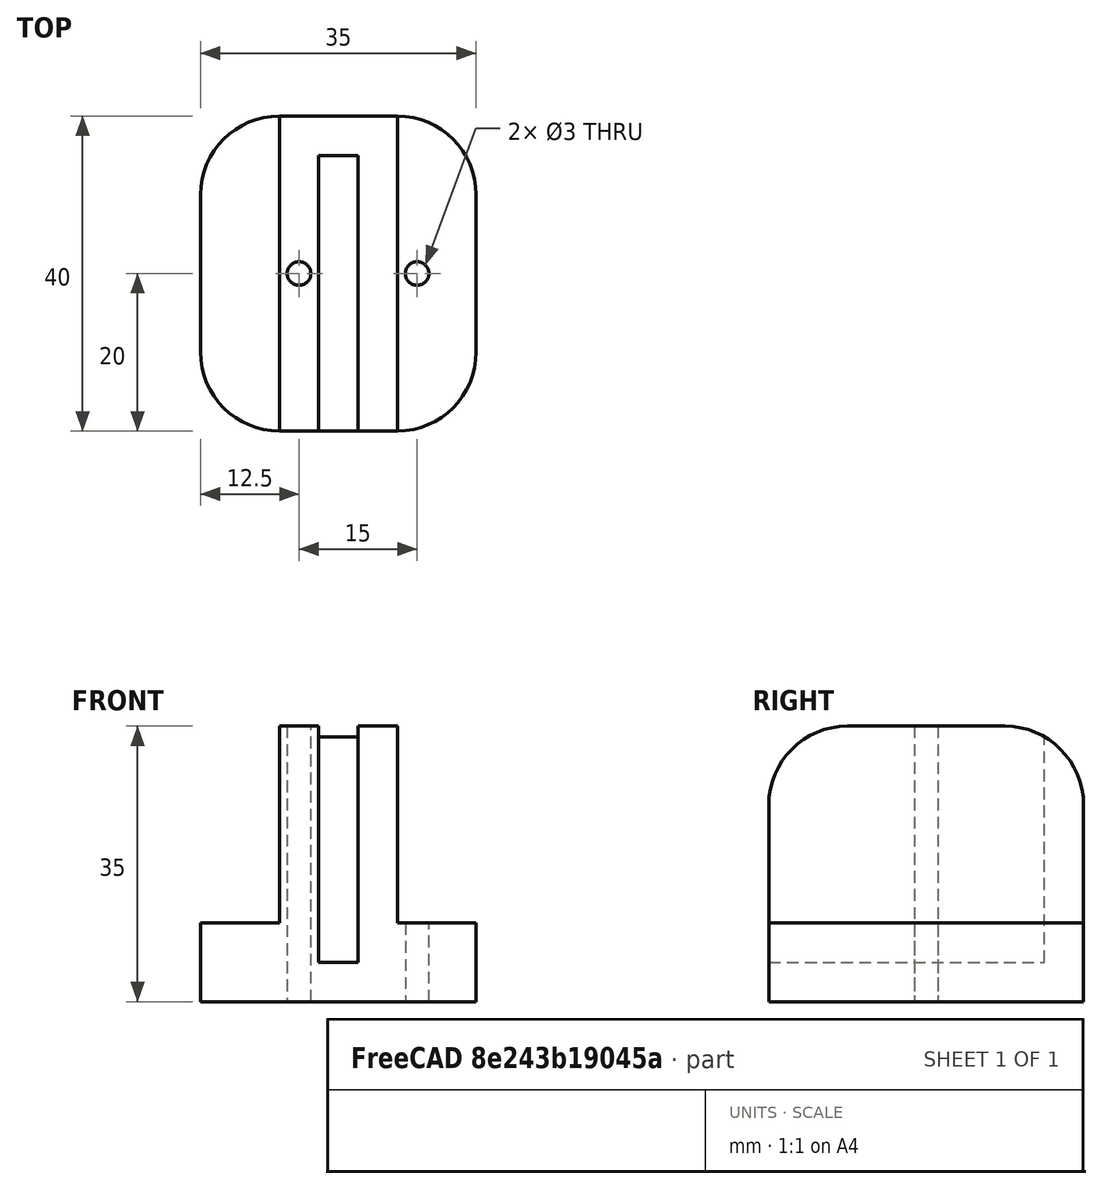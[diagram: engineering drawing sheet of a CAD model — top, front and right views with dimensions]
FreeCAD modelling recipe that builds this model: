
FCSTD DOCUMENT  (FreeCAD 0.21R33771 (Git))
Label: bidee-holder
License: All rights reserved
LicenseURL: https://en.wikipedia.org/wiki/All_rights_reserved
objects: Part::Cut×5, Part::Box×4, Part::Cylinder×2, Part::Fillet×1
note: 12 computed .brp shape members not serialized (recipe doc carries the construction recipe); baked Part::Feature solids carry a one-line shape summary decoded from their .brp

FEATURE [Part::Box] Box  label="Cube"
  AttacherType = Attacher::AttachEngine3D
  Height = 35
  Length = 35
  Width = 40
FEATURE [Part::Fillet] Fillet
  Base = -> Box
  Edges = 6 edges r=10: [Edge1,Edge3,Edge5,Edge7,Edge10,Edge12]
FEATURE [Part::Box] Box001  label="Cube001"
  AttacherType = Attacher::AttachEngine3D
  Height = 25
  Length = 10
  Placement = pos=(0,0,10) rot=(0,0,1;0rad)
  Width = 40
FEATURE [Part::Cut] Cut
  Base = -> Fillet
  Tool = -> Box001
FEATURE [Part::Box] Box002  label="Cube002"
  AttacherType = Attacher::AttachEngine3D
  Height = 35
  Length = 5
  Placement = pos=(15,0,5) rot=(0,0,1;0rad)
  Width = 35
FEATURE [Part::Cut] Cut001
  Base = -> Cut
  Tool = -> Box002
FEATURE [Part::Box] Box003  label="Cube003"
  AttacherType = Attacher::AttachEngine3D
  Height = 25
  Length = 10
  Placement = pos=(25,0,10) rot=(0,0,1;0rad)
  Width = 40
FEATURE [Part::Cut] Cut002
  Base = -> Cut001
  Tool = -> Box003
FEATURE [Part::Cylinder] Cylinder
  Angle = 360
  AttacherType = Attacher::AttachEngine3D
  FirstAngle = 0
  Height = 40
  Placement = pos=(12.5,20,0) rot=(0,0,1;0rad)
  Radius = 1.5
  SecondAngle = 0
FEATURE [Part::Cut] Cut003
  Base = -> Cut002
  Tool = -> Cylinder
FEATURE [Part::Cylinder] Cylinder001
  Angle = 360
  AttacherType = Attacher::AttachEngine3D
  FirstAngle = 0
  Height = 40
  Placement = pos=(27.5,20,0) rot=(0,0,1;0rad)
  Radius = 1.5
  SecondAngle = 0
FEATURE [Part::Cut] Cut004
  Base = -> Cut003
  Tool = -> Cylinder001
